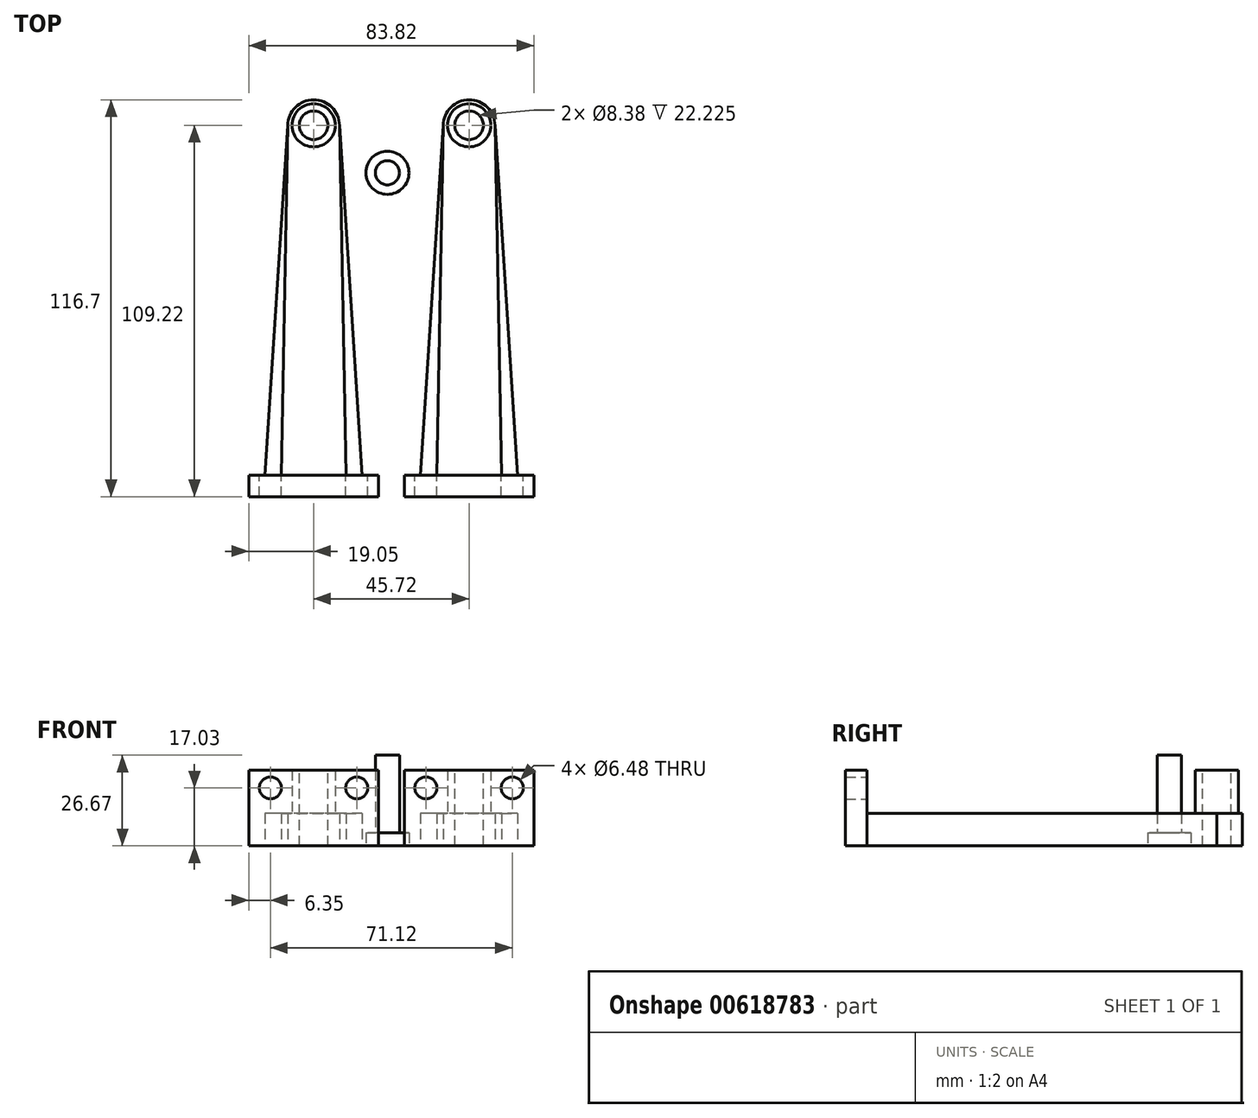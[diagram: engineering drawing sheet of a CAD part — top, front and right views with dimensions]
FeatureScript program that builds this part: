
annotation { "Feature Type Name" : "Feature", "Feature Type Description" : "" }
export const myFeature = defineFeature(function(context is Context, id is Id, definition is map)
    precondition{}
    {
        {
            var Q0;
            Q0=qCreatedBy(makeId("Top.planeOp"),FACE);
            var sketch = newSketch(context, id + "F0", { "sketchPlane" : qUnion([Q0])});
            skCircle(sketch, "E0", {"center": v(0, 109.22) * mm, "radius": 6.35 * mm});
            skLineSegment(sketch, "E1.bottom", {"start": v(0, 0) * mm, "end": v(19.05, 0) * mm});
            skLineSegment(sketch, "E1.top", {"start": v(0, 6.35) * mm, "end": v(19.05, 6.35) * mm});
            skLineSegment(sketch, "E1.right", {"start": v(19.05, 0) * mm, "end": v(19.05, 6.35) * mm});
            skPoint(sketch, "E2.oppositeSnap0", {"position": v(9.53, 0) * mm});
            skLineSegment(sketch, "E2.bottom", {"start": v(0, 6.35) * mm, "end": v(-19.05, 6.35) * mm});
            skLineSegment(sketch, "E2.top", {"start": v(0, 0) * mm, "end": v(-19.05, 0) * mm});
            skLineSegment(sketch, "E2.right", {"start": v(-19.05, 6.35) * mm, "end": v(-19.05, 0) * mm});
            skLineSegment(sketch, "E3", {"start": v(-7.62, 109.22) * mm, "end": v(-9.52, 6.35) * mm});
            skLineSegment(sketch, "E4", {"start": v(-9.52, 6.35) * mm, "end": v(9.52, 6.35) * mm});
            skLineSegment(sketch, "E5", {"start": v(9.52, 6.35) * mm, "end": v(7.62, 109.22) * mm});
            skArc(sketch, "E6", {"start": v(7.62, 109.22) * mm, "mid": v(0, 116.7) * mm, "end": v(-7.62, 109.22) * mm});
            skLineSegment(sketch, "E7.trimOffspring", {"start": v(0, 109.08) * mm, "end": v(0, 109.22) * mm});
            skSolve(sketch);
        }
        {
            var Q0;
            Q0=makeQuery(id+"F0.imprint","IMPRINT",FACE,{"disambiguationData":[TD([[makeQuery(id+"F0.imprint","IMPRINT",EDGE,{"derivedFrom":sQuery(id+"F0.wireOp",EDGE,"E0")}),1.0]])]});
            var Q1;
            Q1=sQuery(id+"F0.wireOp",EDGE,"E0");
            extrude(context, id + "F1", {"entities" : qUnion([Q0]), "surfaceEntities" : qUnion([Q1]), "depth" : 22.22 * mm, "offsetDistance" : 25.4 * mm});
        }
        {
            var Q0;
            Q0 = qSketchRegion(id + "F0", true);
            extrude(context, id + "F2", {"entities" : qUnion([Q0]), "operationType" : NewBodyOperationType.ADD, "depth" : 9.52 * mm, "offsetDistance" : 25.4 * mm});
        }
        {
            var Q0;
            Q0=makeQuery(id+"F2.opExtrude","CAP_FACE",FACE,{"disambiguationData":[OSD([sQuery(id+"F0.wireOp",EDGE,"E0"),sQuery(id+"F0.wireOp",EDGE,"E1.bottom"),sQuery(id+"F0.wireOp",EDGE,"E1.top"),sQuery(id+"F0.wireOp",EDGE,"E1.right"),sQuery(id+"F0.wireOp",EDGE,"E2.bottom"),sQuery(id+"F0.wireOp",EDGE,"E2.top"),sQuery(id+"F0.wireOp",EDGE,"E2.right"),sQuery(id+"F0.wireOp",EDGE,"E3"),sQuery(id+"F0.wireOp",EDGE,"E5"),sQuery(id+"F0.wireOp",EDGE,"E6")])],"isStart":false});
            var sketch = newSketch(context, id + "F3", { "sketchPlane" : qUnion([Q0])});
            skLineSegment(sketch, "E8.bottom", {"start": v(-19.05, 6.35) * mm, "end": v(19.05, 6.35) * mm});
            skLineSegment(sketch, "E8.top", {"start": v(-19.05, 0) * mm, "end": v(19.05, 0) * mm});
            skLineSegment(sketch, "E8.left", {"start": v(-19.05, 6.35) * mm, "end": v(-19.05, 0) * mm});
            skLineSegment(sketch, "E8.right", {"start": v(19.05, 6.35) * mm, "end": v(19.05, 0) * mm});
            skSolve(sketch);
        }
        {
            var Q0;
            Q0=makeQuery(id+"F3.imprint","IMPRINT",FACE,{"disambiguationData":[TD([[makeQuery(id+"F3.imprint","IMPRINT",EDGE,{"derivedFrom":sQuery(id+"F3.wireOp",EDGE,"E8.top")}),-1.0]])]});
            extrude(context, id + "F4", {"entities" : qUnion([Q0]), "operationType" : NewBodyOperationType.ADD, "depth" : 12.7 * mm, "offsetDistance" : 25.4 * mm});
        }
        {
            var Q0;
            {var subQ0=sQuery(id+"F0.wireOp",EDGE,"E0");Q0=makeQuery(id+"F2.boolean.opBoolean","MERGE",FACE,{"derivedFrom":[makeQuery(id+"F1.opExtrude","CAP_FACE",FACE,{"disambiguationData":[OSD([subQ0])],"isStart":true}),makeQuery(id+"F2.opExtrude","CAP_FACE",FACE,{"disambiguationData":[OSD([subQ0,sQuery(id+"F0.wireOp",EDGE,"E1.bottom"),sQuery(id+"F0.wireOp",EDGE,"E1.top"),sQuery(id+"F0.wireOp",EDGE,"E1.right"),sQuery(id+"F0.wireOp",EDGE,"E2.bottom"),sQuery(id+"F0.wireOp",EDGE,"E2.top"),sQuery(id+"F0.wireOp",EDGE,"E2.right"),sQuery(id+"F0.wireOp",EDGE,"E3"),sQuery(id+"F0.wireOp",EDGE,"E5"),sQuery(id+"F0.wireOp",EDGE,"E6")])],"isStart":true})]});}
            var sketch = newSketch(context, id + "F5", { "sketchPlane" : qUnion([Q0])});
            skLineSegment(sketch, "E9", {"start": v(-7.62, -109.22) * mm, "end": v(-14.29, -6.35) * mm});
            skLineSegment(sketch, "E10", {"start": v(-14.29, -6.35) * mm, "end": v(14.29, -6.35) * mm});
            skLineSegment(sketch, "E11", {"start": v(14.29, -6.35) * mm, "end": v(7.62, -109.22) * mm});
            skLineSegment(sketch, "E12", {"start": v(7.62, -109.22) * mm, "end": v(-7.62, -109.22) * mm});
            skSolve(sketch);
        }
        {
            var Q0;
            {var subQ2=sQuery(id+"F5.wireOp",EDGE,"E11");Q0=makeQuery(id+"F5.imprint","IMPRINT",FACE,{"disambiguationData":[TD([[makeQuery(id+"F5.imprint","IMPRINT",EDGE,{"derivedFrom":subQ2}),-1.0]])]});}
            var Q1;
            {var subQ0=sQuery(id+"F5.wireOp",EDGE,"E9");Q1=makeQuery(id+"F5.imprint","IMPRINT",FACE,{"disambiguationData":[TD([[makeQuery(id+"F5.imprint","IMPRINT",EDGE,{"derivedFrom":subQ0}),-1.0]])]});}
            extrude(context, id + "F6", {"entities" : qUnion([Q0, Q1]), "oppositeDirection" : true, "depth" : 9.52 * mm, "offsetDistance" : 25.4 * mm});
        }
        {
            var Q0;
            Q0=makeQuery(id+"F4.boolean.opBoolean","MERGE",FACE,{"derivedFrom":[makeQuery(id+"F2.opExtrude","SWEPT_FACE",FACE,{"disambiguationData":[OSD([sQuery(id+"F0.wireOp",EDGE,"E1.top")])]}),makeQuery(id+"F2.opExtrude","SWEPT_FACE",FACE,{"disambiguationData":[OSD([sQuery(id+"F0.wireOp",EDGE,"E2.bottom")])]}),makeQuery(id+"F4.opExtrude","SWEPT_FACE",FACE,{"disambiguationData":[OSD([sQuery(id+"F3.wireOp",EDGE,"E8.bottom")])]})]});
            var sketch = newSketch(context, id + "F7", { "sketchPlane" : qUnion([Q0])});
            skLineSegment(sketch, "E13", {"start": v(-19.05, 17.03) * mm, "end": v(-12.7, 17.03) * mm});
            skLineSegment(sketch, "E14", {"start": v(19.05, 17.03) * mm, "end": v(12.7, 17.03) * mm});
            skSolve(sketch);
        }
        {
            var Q0;
            Q0=sQuery(id+"F7.wireOp",VERTEX,"E14.end");
            var Q1;
            Q1=sQuery(id+"F7.wireOp",VERTEX,"E13.end");
            var Q2;
            Q2=makeQuery(id+"F1.opExtrude","SWEPT_BODY",BODY,{"disambiguationData":[OSD([sQuery(id+"F0.wireOp",EDGE,"E0")])]});
            hole(context, id + "F8", {"style" : HoleStyle.SIMPLE, "endStyle" : HoleEndStyle.THROUGH, "holeDiameter" : 6.48 * mm, "majorDiameter" : 6.35 * mm, "isTappedThrough" : true, "tappedDepth" : 12.7 * mm, "tapClearance" : 3, "locations" : qUnion([Q0, Q1]), "scope" : qUnion([Q2])});
        }
        {
            var Q0;
            Q0=makeQuery(id+"F6.opExtrude","SWEPT_BODY",BODY,{"disambiguationData":[OSD([sQuery(id+"F0.wireOp",EDGE,"E3"),sQuery(id+"F5.wireOp",EDGE,"E9"),sQuery(id+"F5.wireOp",EDGE,"E10")])]});
            var Q1;
            Q1=makeQuery(id+"F6.opExtrude","SWEPT_BODY",BODY,{"disambiguationData":[OSD([sQuery(id+"F0.wireOp",EDGE,"E5"),sQuery(id+"F5.wireOp",EDGE,"E10"),sQuery(id+"F5.wireOp",EDGE,"E11")])]});
            var Q2;
            Q2=makeQuery(id+"F1.opExtrude","SWEPT_BODY",BODY,{"disambiguationData":[OSD([sQuery(id+"F0.wireOp",EDGE,"E0")])]});
            transform(context, id + "F9", {"entities" : qUnion([Q0, Q1, Q2]), "transformType" : TransformType.TRANSLATION_3D, "dx" : 45.72 * mm, "dy" : 0 * mm, "dz" : 0 * mm, "makeCopy" : true});
        }
        {
            var Q0;
            Q0=makeQuery(id+"F1.opExtrude","CAP_FACE",FACE,{"disambiguationData":[OSD([sQuery(id+"F0.wireOp",EDGE,"E0")])],"isStart":false});
            var sketch = newSketch(context, id + "F10", { "sketchPlane" : qUnion([Q0])});
            skLineSegment(sketch, "E15", {"start": v(0, 102.87) * mm, "end": v(0, 109.22) * mm});
            skSolve(sketch);
        }
        {
            var Q0;
            Q0=makeQuery(id+"F9.opPattern","COPY",FACE,{"derivedFrom":makeQuery(id+"F1.opExtrude","CAP_FACE",FACE,{"disambiguationData":[OSD([sQuery(id+"F0.wireOp",EDGE,"E0")])],"isStart":false}),"instanceName":"1"});
            var sketch = newSketch(context, id + "F11", { "sketchPlane" : qUnion([Q0])});
            skLineSegment(sketch, "E16", {"start": v(46, 102.88) * mm, "end": v(45.72, 109.22) * mm});
            skSolve(sketch);
        }
        {
            var Q0;
            Q0=sQuery(id+"F10.wireOp",VERTEX,"E15.end");
            var Q1;
            Q1=sQuery(id+"F11.wireOp",VERTEX,"E16.end");
            var Q2;
            Q2=makeQuery(id+"F1.opExtrude","SWEPT_BODY",BODY,{"disambiguationData":[OSD([sQuery(id+"F0.wireOp",EDGE,"E0")])]});
            var Q3;
            Q3=makeQuery(id+"F9.opPattern","COPY",BODY,{"derivedFrom":makeQuery(id+"F1.opExtrude","SWEPT_BODY",BODY,{"disambiguationData":[OSD([sQuery(id+"F0.wireOp",EDGE,"E0")])]}),"instanceName":"1"});
            hole(context, id + "F12", {"style" : HoleStyle.SIMPLE, "endStyle" : HoleEndStyle.THROUGH, "holeDiameter" : 8.38 * mm, "majorDiameter" : 6.35 * mm, "isTappedThrough" : true, "tappedDepth" : 12.7 * mm, "tapClearance" : 3, "locations" : qUnion([Q0, Q1]), "scope" : qUnion([Q2, Q3])});
        }
        {
            var Q0;
            Q0=qCreatedBy(makeId("Top.planeOp"),FACE);
            var sketch = newSketch(context, id + "F13", { "sketchPlane" : qUnion([Q0])});
            skCircle(sketch, "E17", {"center": v(21.7, 95.26) * mm, "radius": 6.35 * mm});
            skSolve(sketch);
        }
        {
            var Q0;
            Q0 = qSketchRegion(id + "F13", true);
            extrude(context, id + "F14", {"entities" : qUnion([Q0]), "depth" : 3.8 * mm, "offsetDistance" : 25.4 * mm});
        }
        {
            var Q0;
            Q0=makeQuery(id+"F14.opExtrude","CAP_FACE",FACE,{"disambiguationData":[OSD([sQuery(id+"F13.wireOp",EDGE,"E17")])],"isStart":false});
            var sketch = newSketch(context, id + "F15", { "sketchPlane" : qUnion([Q0])});
            skCircle(sketch, "E18", {"center": v(21.7, 95.26) * mm, "radius": 3.56 * mm});
            skSolve(sketch);
        }
        {
            var Q0;
            Q0 = qSketchRegion(id + "F15", true);
            extrude(context, id + "F16", {"entities" : qUnion([Q0]), "operationType" : NewBodyOperationType.ADD, "depth" : 22.86 * mm, "offsetDistance" : 25.4 * mm});
        }
    });
